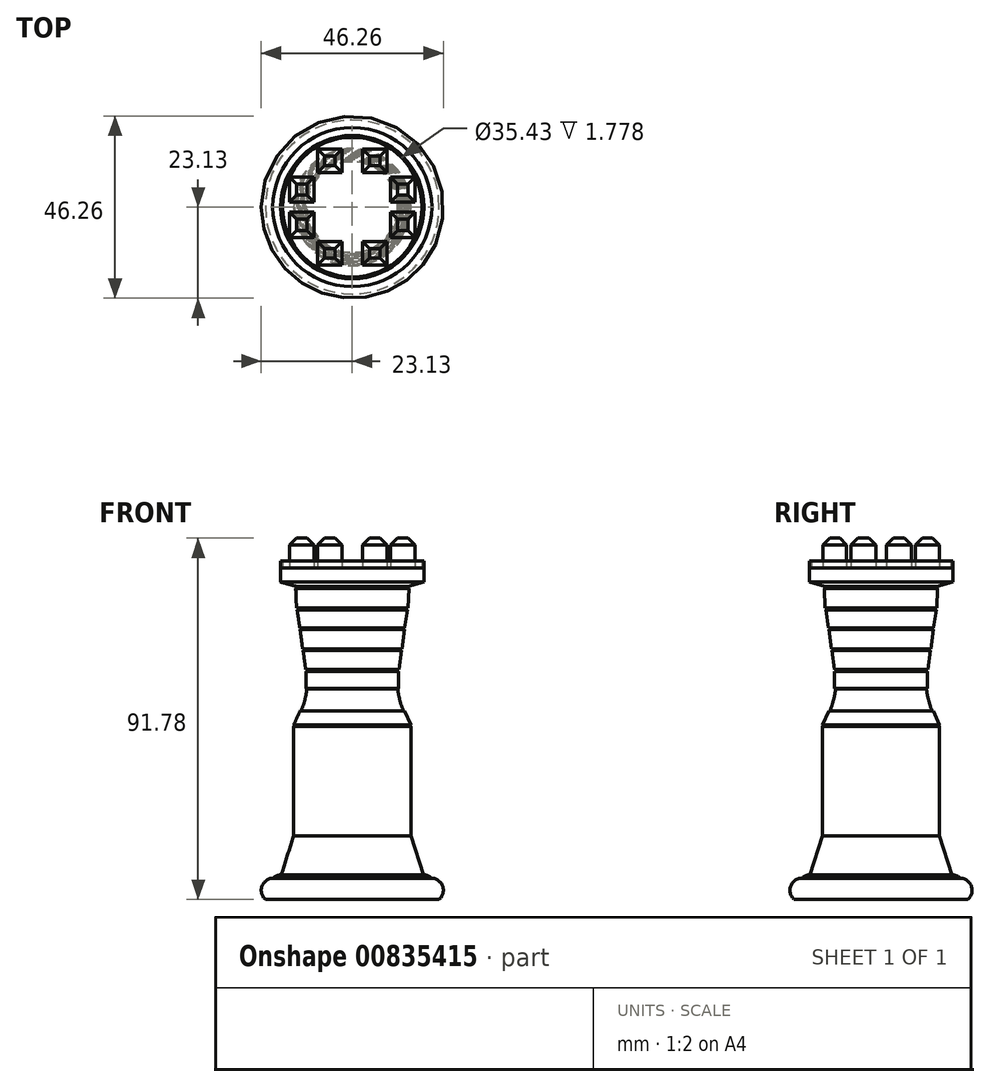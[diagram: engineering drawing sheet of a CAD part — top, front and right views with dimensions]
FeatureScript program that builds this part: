
annotation { "Feature Type Name" : "Feature", "Feature Type Description" : "" }
export const myFeature = defineFeature(function(context is Context, id is Id, definition is map)
    precondition{}
    {
        {
            var Q0;
            Q0=qCreatedBy(makeId("Front.planeOp"),FACE);
            var sketch = newSketch(context, id + "F0", { "sketchPlane" : qUnion([Q0])});
            skLineSegment(sketch, "E0", {"start": v(0, -37.92) * mm, "end": v(0, 40) * mm});
            skFitSpline(sketch, "E1.trimOffspring", {"points": [v(-25.61, -37.92) * mm, v(-19.46, -8.96) * mm, v(-11.68, 8.42) * mm, v(-14.2, 35.39) * mm, v(-12.94, 57.3) * mm, v(-15.84, 63.8) * mm], "startDerivative": vector(16.77, 129.7) * mm, "endDerivative": vector(-31.89, 45.75) * mm});
            skArc(sketch, "E2", {"start": v(-19.03, -13.92) * mm, "mid": v(-18.97, -13.76) * mm, "end": v(-18.92, -13.6) * mm});
            skArc(sketch, "E3", {"start": v(-18.05, -37.92) * mm, "mid": v(-21.18, -41.05) * mm, "end": v(-18.05, -44.17) * mm});
            skArc(sketch, "E4", {"start": v(-20.2, -38.78) * mm, "mid": v(-22.96, -40.84) * mm, "end": v(-22.07, -44.17) * mm});
            skLineSegment(sketch, "E5", {"start": v(-18.05, -44.17) * mm, "end": v(0, -44.17) * mm});
            skLineSegment(sketch, "E6", {"start": v(0, -44.17) * mm, "end": v(0, -37.92) * mm});
            skLineSegment(sketch, "E7", {"start": v(-18.05, -44.17) * mm, "end": v(-22.07, -44.17) * mm});
            skLineSegment(sketch, "E8", {"start": v(-14.2, 38.6) * mm, "end": v(-14.63, 40) * mm});
            skPoint(sketch, "E9.orphan", {"position": v(-21.75, 63.8) * mm});
            skPoint(sketch, "E10.start.orphan", {"position": v(-18.85, 54.11) * mm});
            skLineSegment(sketch, "E11", {"start": v(-14.2, 35.39) * mm, "end": v(-18.21, 36.46) * mm});
            skLineSegment(sketch, "E12", {"start": v(-18.21, 36.46) * mm, "end": v(-18.21, 40) * mm});
            skLineSegment(sketch, "E13", {"start": v(-18.21, 40) * mm, "end": v(0, 40) * mm});
            skPoint(sketch, "E14.end.orphan", {"position": v(-17.98, 51.2) * mm});
            skPoint(sketch, "E15.end.orphan", {"position": v(-18.85, 60.36) * mm});
            skPoint(sketch, "E16.start.orphan", {"position": v(-15.84, 69.76) * mm});
            skPoint(sketch, "E17.end.orphan", {"position": v(0, 63.8) * mm});
            skPoint(sketch, "E17.start.orphan", {"position": v(0, 69.76) * mm});
            skLineSegment(sketch, "E18", {"start": v(-19.74, -30.2) * mm, "end": v(-20.45, -30.2) * mm});
            skLineSegment(sketch, "E19", {"start": v(-19.74, -24.35) * mm, "end": v(-19.12, -24.43) * mm});
            skLineSegment(sketch, "E20", {"start": v(-19.3, -19.44) * mm, "end": v(-18.9, -19.49) * mm});
            skLineSegment(sketch, "E21", {"start": v(-19.09, -24) * mm, "end": v(-19.64, -23.96) * mm});
            skLineSegment(sketch, "E22", {"start": v(-18.9, -19.08) * mm, "end": v(-19.3, -19.08) * mm});
            skLineSegment(sketch, "E23", {"start": v(-19.3, -15.27) * mm, "end": v(-18.96, -15.27) * mm});
            skLineSegment(sketch, "E24", {"start": v(-18.92, -13.6) * mm, "end": v(-19.33, -13.6) * mm});
            skLineSegment(sketch, "E25", {"start": v(-18.2, -9.68) * mm, "end": v(-17.85, -9.68) * mm});
            skLineSegment(sketch, "E26", {"start": v(-17.8, -9.44) * mm, "end": v(-18.1, -9.44) * mm});
            skLineSegment(sketch, "E27", {"start": v(-17.58, -5.85) * mm, "end": v(-17.26, -5.85) * mm});
            skLineSegment(sketch, "E28", {"start": v(-16.67, -3.48) * mm, "end": v(-17.07, -3.48) * mm});
            skLineSegment(sketch, "E29", {"start": v(-15.23, -0.26) * mm, "end": v(-14.89, -0.26) * mm});
            skLineSegment(sketch, "E30", {"start": v(-14.65, 0.19) * mm, "end": v(-14.89, 0.19) * mm});
            skLineSegment(sketch, "E31", {"start": v(-14.89, 0.19) * mm, "end": v(-13.3, 3.71) * mm});
            skLineSegment(sketch, "E32", {"start": v(-13.3, 3.71) * mm, "end": v(-12.99, 3.71) * mm});
            skLineSegment(sketch, "E33", {"start": v(-12.84, 4.1) * mm, "end": v(-13.15, 4.1) * mm});
            skLineSegment(sketch, "E34", {"start": v(-13.15, 4.1) * mm, "end": v(-11.9, 8.96) * mm});
            skLineSegment(sketch, "E35", {"start": v(-11.9, 8.96) * mm, "end": v(-11.68, 8.96) * mm});
            skLineSegment(sketch, "E36", {"start": v(-11.56, 9.35) * mm, "end": v(-11.8, 9.41) * mm});
            skLineSegment(sketch, "E37", {"start": v(-11.8, 9.41) * mm, "end": v(-11.8, 13.74) * mm});
            skLineSegment(sketch, "E38", {"start": v(-11.8, 13.74) * mm, "end": v(-11.5, 13.74) * mm});
            skLineSegment(sketch, "E39", {"start": v(-11.53, 14.22) * mm, "end": v(-11.85, 14.22) * mm});
            skLineSegment(sketch, "E40", {"start": v(-11.85, 14.22) * mm, "end": v(-12.48, 19.05) * mm});
            skLineSegment(sketch, "E41", {"start": v(-12.48, 19.05) * mm, "end": v(-12.09, 19.1) * mm});
            skLineSegment(sketch, "E42", {"start": v(-12.15, 19.51) * mm, "end": v(-12.62, 19.51) * mm});
            skLineSegment(sketch, "E43", {"start": v(-12.62, 19.51) * mm, "end": v(-13.26, 24.38) * mm});
            skLineSegment(sketch, "E44", {"start": v(-13.26, 24.38) * mm, "end": v(-12.93, 24.42) * mm});
            skLineSegment(sketch, "E45", {"start": v(-13, 24.84) * mm, "end": v(-13.32, 24.84) * mm});
            skLineSegment(sketch, "E46", {"start": v(-13.32, 24.84) * mm, "end": v(-14.01, 29.33) * mm});
            skLineSegment(sketch, "E47", {"start": v(-14.01, 29.33) * mm, "end": v(-13.68, 29.38) * mm});
            skLineSegment(sketch, "E48", {"start": v(-13.75, 29.9) * mm, "end": v(-14.19, 29.9) * mm});
            skLineSegment(sketch, "E49", {"start": v(-14.19, 29.9) * mm, "end": v(-14.38, 34.86) * mm});
            skLineSegment(sketch, "E50", {"start": v(-14.38, 34.86) * mm, "end": v(-14.19, 34.87) * mm});
            skLineSegment(sketch, "E51", {"start": v(-14.19, 34.87) * mm, "end": v(-14.2, 35.39) * mm});
            skLineSegment(sketch, "E52", {"start": v(-14.89, -0.26) * mm, "end": v(-14.89, -27.96) * mm});
            skLineSegment(sketch, "E53", {"start": v(-14.89, -27.96) * mm, "end": v(-18.05, -37.92) * mm});
            skArc(sketch, "E54.trimOffspring", {"start": v(-18.9, -19.49) * mm, "mid": v(-18.9, -19.28) * mm, "end": v(-18.9, -19.08) * mm});
            skArc(sketch, "E55.trimOffspring", {"start": v(-17.85, -9.68) * mm, "mid": v(-17.83, -9.56) * mm, "end": v(-17.8, -9.44) * mm});
            skSolve(sketch);
        }
        {
            var Q0;
            Q0=qSketchRegion(id+"F0",true);
            var Q1;
            Q1=sQuery(id+"F0.wireOp",EDGE,"E0");
            revolve(context, id + "F1", {"surfaceOperationType" : NewSurfaceOperationType.NEW, "entities" : qUnion([Q0]), "axis" : qUnion([Q1]), "revolveType" : RevolveType.FULL});
        }
        {
            var Q0;
            Q0=makeQuery(id+"F1.opRevolve","SWEPT_FACE",FACE,{"disambiguationData":[OSD([sQuery(id+"F0.wireOp",EDGE,"E13")])]});
            var sketch = newSketch(context, id + "F2", { "sketchPlane" : qUnion([Q0])});
            skLineSegment(sketch, "E56", {"start": v(0, 31.2) * mm, "end": v(0, -32.37) * mm});
            skLineSegment(sketch, "E57", {"start": v(-39, 0) * mm, "end": v(37.48, 0) * mm});
            skLineSegment(sketch, "E58.bottom", {"start": v(-2.65, 14.77) * mm, "end": v(-8.77, 14.77) * mm});
            skLineSegment(sketch, "E58.top", {"start": v(-2.65, 8.73) * mm, "end": v(-8.77, 8.73) * mm});
            skLineSegment(sketch, "E58.left", {"start": v(-2.65, 14.77) * mm, "end": v(-2.65, 8.73) * mm});
            skLineSegment(sketch, "E58.right", {"start": v(-8.77, 14.77) * mm, "end": v(-8.77, 8.73) * mm});
            skLineSegment(sketch, "E59.MirrorCS", {"start": v(2.65, 14.77) * mm, "end": v(2.65, 8.73) * mm});
            skLineSegment(sketch, "E60.MirrorCS", {"start": v(2.65, 14.77) * mm, "end": v(8.77, 14.77) * mm});
            skLineSegment(sketch, "E61.MirrorCS", {"start": v(8.77, 14.77) * mm, "end": v(8.77, 8.73) * mm});
            skLineSegment(sketch, "E62.MirrorCS", {"start": v(2.65, 8.73) * mm, "end": v(8.77, 8.73) * mm});
            skLineSegment(sketch, "E63.MirrorCS", {"start": v(-2.65, -8.73) * mm, "end": v(-8.77, -8.73) * mm});
            skLineSegment(sketch, "E64.MirrorCS", {"start": v(-8.77, -14.77) * mm, "end": v(-8.77, -8.73) * mm});
            skLineSegment(sketch, "E65.MirrorCS", {"start": v(-2.65, -14.77) * mm, "end": v(-2.65, -8.73) * mm});
            skLineSegment(sketch, "E66.MirrorCS", {"start": v(2.65, -8.73) * mm, "end": v(8.77, -8.73) * mm});
            skLineSegment(sketch, "E67.MirrorCS", {"start": v(8.77, -14.77) * mm, "end": v(8.77, -8.73) * mm});
            skLineSegment(sketch, "E68.MirrorCS", {"start": v(2.65, -14.77) * mm, "end": v(2.65, -8.73) * mm});
            skLineSegment(sketch, "E69.MirrorCS", {"start": v(-2.65, -14.77) * mm, "end": v(-8.77, -14.77) * mm});
            skLineSegment(sketch, "E70.MirrorCS", {"start": v(2.65, -14.77) * mm, "end": v(8.77, -14.77) * mm});
            skLineSegment(sketch, "E71.bottom", {"start": v(9.68, 7.68) * mm, "end": v(15.88, 7.68) * mm});
            skLineSegment(sketch, "E71.top", {"start": v(9.68, 1.31) * mm, "end": v(15.88, 1.31) * mm});
            skLineSegment(sketch, "E71.left", {"start": v(9.68, 7.68) * mm, "end": v(9.68, 1.31) * mm});
            skLineSegment(sketch, "E71.right", {"start": v(15.88, 7.68) * mm, "end": v(15.88, 1.31) * mm});
            skLineSegment(sketch, "E72.MirrorCS", {"start": v(-9.68, 7.68) * mm, "end": v(-9.68, 1.31) * mm});
            skLineSegment(sketch, "E73.MirrorCS", {"start": v(-9.68, 7.68) * mm, "end": v(-15.88, 7.68) * mm});
            skLineSegment(sketch, "E74.MirrorCS", {"start": v(-9.68, 1.31) * mm, "end": v(-15.88, 1.31) * mm});
            skLineSegment(sketch, "E75.MirrorCS", {"start": v(-15.88, 7.68) * mm, "end": v(-15.88, 1.31) * mm});
            skLineSegment(sketch, "E76.MirrorCS", {"start": v(-9.68, -7.68) * mm, "end": v(-9.68, -1.31) * mm});
            skLineSegment(sketch, "E77.MirrorCS", {"start": v(-9.68, -7.68) * mm, "end": v(-15.88, -7.68) * mm});
            skLineSegment(sketch, "E78.MirrorCS", {"start": v(-9.68, -1.31) * mm, "end": v(-15.88, -1.31) * mm});
            skLineSegment(sketch, "E79.MirrorCS", {"start": v(-15.88, -7.68) * mm, "end": v(-15.88, -1.31) * mm});
            skLineSegment(sketch, "E80.MirrorCS", {"start": v(9.68, -1.31) * mm, "end": v(15.88, -1.31) * mm});
            skLineSegment(sketch, "E81.MirrorCS", {"start": v(9.68, -7.68) * mm, "end": v(9.68, -1.31) * mm});
            skLineSegment(sketch, "E82.MirrorCS", {"start": v(9.68, -7.68) * mm, "end": v(15.88, -7.68) * mm});
            skLineSegment(sketch, "E83.MirrorCS", {"start": v(15.88, -7.68) * mm, "end": v(15.88, -1.31) * mm});
            skSolve(sketch);
        }
        {
            var Q0;
            Q0=makeQuery(id+"F2.imprint","IMPRINT",FACE,{"disambiguationData":[TD([[makeQuery(id+"F2.imprint","IMPRINT",EDGE,{"derivedFrom":sQuery(id+"F2.wireOp",EDGE,"E72.MirrorCS")}),-1.0]])]});
            var Q1;
            Q1=makeQuery(id+"F2.imprint","IMPRINT",FACE,{"disambiguationData":[TD([[makeQuery(id+"F2.imprint","IMPRINT",EDGE,{"derivedFrom":sQuery(id+"F2.wireOp",EDGE,"E58.bottom")}),1.0]])]});
            var Q2;
            Q2=makeQuery(id+"F2.imprint","IMPRINT",FACE,{"disambiguationData":[TD([[makeQuery(id+"F2.imprint","IMPRINT",EDGE,{"derivedFrom":sQuery(id+"F2.wireOp",EDGE,"E59.MirrorCS")}),1.0]])]});
            var Q3;
            Q3=makeQuery(id+"F2.imprint","IMPRINT",FACE,{"disambiguationData":[TD([[makeQuery(id+"F2.imprint","IMPRINT",EDGE,{"derivedFrom":sQuery(id+"F2.wireOp",EDGE,"E71.bottom")}),-1.0]])]});
            var Q4;
            Q4=makeQuery(id+"F2.imprint","IMPRINT",FACE,{"disambiguationData":[TD([[makeQuery(id+"F2.imprint","IMPRINT",EDGE,{"derivedFrom":sQuery(id+"F2.wireOp",EDGE,"E80.MirrorCS")}),-1.0]])]});
            var Q5;
            Q5=makeQuery(id+"F2.imprint","IMPRINT",FACE,{"disambiguationData":[TD([[makeQuery(id+"F2.imprint","IMPRINT",EDGE,{"derivedFrom":sQuery(id+"F2.wireOp",EDGE,"E67.MirrorCS")}),1.0]])]});
            var Q6;
            Q6=makeQuery(id+"F2.imprint","IMPRINT",FACE,{"disambiguationData":[TD([[makeQuery(id+"F2.imprint","IMPRINT",EDGE,{"derivedFrom":sQuery(id+"F2.wireOp",EDGE,"E64.MirrorCS")}),-1.0]])]});
            var Q7;
            Q7=makeQuery(id+"F2.imprint","IMPRINT",FACE,{"disambiguationData":[TD([[makeQuery(id+"F2.imprint","IMPRINT",EDGE,{"derivedFrom":sQuery(id+"F2.wireOp",EDGE,"E76.MirrorCS")}),1.0]])]});
            extrude(context, id + "F3", {"entities" : qUnion([Q0, Q1, Q2, Q3, Q4, Q5, Q6, Q7]), "operationType" : NewBodyOperationType.ADD, "depth" : 7.62 * mm, "offsetDistance" : 25.4 * mm});
        }
        {
            var Q0;
            Q0=makeQuery(id+"F1.opRevolve","SWEPT_FACE",FACE,{"disambiguationData":[OSD([sQuery(id+"F0.wireOp",EDGE,"E13")])]});
            var sketch = newSketch(context, id + "F4", { "sketchPlane" : qUnion([Q0])});
            skCircle(sketch, "E84", {"center": v(0, 0) * mm, "radius": 18.21 * mm});
            skCircle(sketch, "E85", {"center": v(0, 0) * mm, "radius": 17.72 * mm});
            skSolve(sketch);
        }
        {
            var Q0;
            Q0 = qSketchRegion(id + "F4", true);
            extrude(context, id + "F5", {"entities" : qUnion([Q0]), "operationType" : NewBodyOperationType.ADD, "depth" : 1.78 * mm, "offsetDistance" : 25.4 * mm});
        }
        {
            var Q0;
            Q0=makeQuery(id+"F3.opExtrude","CAP_FACE",FACE,{"disambiguationData":[OSD([sQuery(id+"F2.wireOp",EDGE,"E76.MirrorCS"),sQuery(id+"F2.wireOp",EDGE,"E77.MirrorCS"),sQuery(id+"F2.wireOp",EDGE,"E78.MirrorCS"),sQuery(id+"F2.wireOp",EDGE,"E79.MirrorCS")])],"isStart":false});
            var Q1;
            Q1=makeQuery(id+"F3.opExtrude","CAP_FACE",FACE,{"disambiguationData":[OSD([sQuery(id+"F2.wireOp",EDGE,"E72.MirrorCS"),sQuery(id+"F2.wireOp",EDGE,"E73.MirrorCS"),sQuery(id+"F2.wireOp",EDGE,"E74.MirrorCS"),sQuery(id+"F2.wireOp",EDGE,"E75.MirrorCS")])],"isStart":false});
            var Q2;
            Q2=makeQuery(id+"F3.opExtrude","CAP_FACE",FACE,{"disambiguationData":[OSD([sQuery(id+"F2.wireOp",EDGE,"E58.bottom"),sQuery(id+"F2.wireOp",EDGE,"E58.top"),sQuery(id+"F2.wireOp",EDGE,"E58.left"),sQuery(id+"F2.wireOp",EDGE,"E58.right")])],"isStart":false});
            var Q3;
            Q3=makeQuery(id+"F3.opExtrude","CAP_FACE",FACE,{"disambiguationData":[OSD([sQuery(id+"F2.wireOp",EDGE,"E59.MirrorCS"),sQuery(id+"F2.wireOp",EDGE,"E60.MirrorCS"),sQuery(id+"F2.wireOp",EDGE,"E61.MirrorCS"),sQuery(id+"F2.wireOp",EDGE,"E62.MirrorCS")])],"isStart":false});
            var Q4;
            Q4=makeQuery(id+"F3.opExtrude","CAP_FACE",FACE,{"disambiguationData":[OSD([sQuery(id+"F2.wireOp",EDGE,"E71.bottom"),sQuery(id+"F2.wireOp",EDGE,"E71.top"),sQuery(id+"F2.wireOp",EDGE,"E71.left"),sQuery(id+"F2.wireOp",EDGE,"E71.right")])],"isStart":false});
            var Q5;
            Q5=makeQuery(id+"F3.opExtrude","CAP_FACE",FACE,{"disambiguationData":[OSD([sQuery(id+"F2.wireOp",EDGE,"E80.MirrorCS"),sQuery(id+"F2.wireOp",EDGE,"E81.MirrorCS"),sQuery(id+"F2.wireOp",EDGE,"E82.MirrorCS"),sQuery(id+"F2.wireOp",EDGE,"E83.MirrorCS")])],"isStart":false});
            var Q6;
            Q6=makeQuery(id+"F3.opExtrude","CAP_FACE",FACE,{"disambiguationData":[OSD([sQuery(id+"F2.wireOp",EDGE,"E67.MirrorCS"),sQuery(id+"F2.wireOp",EDGE,"E68.MirrorCS"),sQuery(id+"F2.wireOp",EDGE,"E66.MirrorCS"),sQuery(id+"F2.wireOp",EDGE,"E70.MirrorCS")])],"isStart":false});
            var Q7;
            Q7=makeQuery(id+"F3.opExtrude","CAP_FACE",FACE,{"disambiguationData":[OSD([sQuery(id+"F2.wireOp",EDGE,"E64.MirrorCS"),sQuery(id+"F2.wireOp",EDGE,"E65.MirrorCS"),sQuery(id+"F2.wireOp",EDGE,"E63.MirrorCS"),sQuery(id+"F2.wireOp",EDGE,"E69.MirrorCS")])],"isStart":false});
            chamfer(context, id + "F6", {"entities" : qUnion([Q0, Q1, Q2, Q3, Q4, Q5, Q6, Q7]), "width" : 1.78 * mm, "tangentPropagation" : true});
        }
    });
